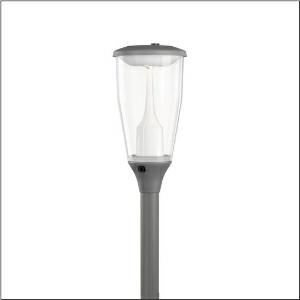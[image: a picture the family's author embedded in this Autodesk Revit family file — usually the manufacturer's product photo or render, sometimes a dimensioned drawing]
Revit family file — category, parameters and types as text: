
# Revit family: dl_11_iq___st1_2a_5xa5565ew14hp00022_746d
name_source: partatom
category: Lighting Fixtures
units: mm (PartAtom-declared; Revit-internal decimal feet)

## family parameters
Cut with Voids When Loaded = No
Host = Face
Light Source = No
Part Type = Normal
Room Calculation Point = No
Round Connector Dimension = Use Diameter
Shared = No

## types (1)
- --- (1 x LED, 4790 lm, 33.5 W, 3000K)
    Apparent Load = 34 VA
    CIE Flux Codes = 23 60 93 95 100
    Color Rendering = 70
    Color Temperature = 3000K
    Default Elevation = 1800 mm
    Description = DL 11 iQ, mast luminaire, Module 540 iQ-SR, primary light control with 3 zone facetted reflector, of plastic, silver coated, highly specular, structured, primary optical cover: cover, of PMMA, transparent, light distribution: ST1.2a, light emission: direct distribution, primary light characteristic: asymmetric, installation type: post-top, LED, High Power LED, rated luminous flux: 4.790lm, luminous efficacy: 143lm/W, light colour: 730, colour temperature: 3000K, control gear: iQ-Street Remote, D4i with power reduction, control: pre-setting: logarithmic dimming characteristic, Street-Remote, Auto-Match, Temp-Guard, Lumen-Switch, Night-Set, Smart-Wire, Light-Fading, Desk-Remote (wireless, voltage-free reading and setting of iQ features in the workshop via application-optimized NFC function/RFID function), optimised constant luminous flux control (CLO 2.0), mains connection: 220..240V, AC, 50/60Hz, connection cable pre-assembled, cable length: 5,5m, start of lifetime: 34W, end of service life: 36W, reduction: 15W, luminaire housing, upper part, of diecast aluminium, coated, SITECO metallic grey (DB 702S), spigot size: 60mm (post-top), mounting height: 3..5m, post-top mast mounting element, of diecast aluminium, coated, SITECO metallic grey (DB 702S), Module 540 iQ-SR, traffic white (RAL 9016), equipment: Power, Smart Interface above and design motion detector below, protection rating (complete): IP65, insulation class (complete): insulation class II (safety insulation), certification: CE, ENEC, ENEC+, VDE, impact resistance: IK07, packaging unit: 1 piece

Light Distribution: ST1.2a
    Height = 665 mm
    Lamp = 1 x LED
    Lamp Light Flux = 4790 lm
    Lamp Power = 33.5 W
    Lamp count = 1
    Length = 334 mm
    Luminous efficacy = 143 lm/W
    Manufacturer = Siteco
    ModVariant = No
    Model = 5XA5565EW14HP00022
    Number of Poles = 1
    OnlyDefault = Yes
    Power Factor = 1
    Product Name = DL 11 iQ | ST1.2a
    Product group = mast luminaire | pylon top
    ProductGroupID = 6100
    Protection Class = Protection class II
    Protection Degree = IP 65
    RLX_Detail_Level = 1
    RLX_Emergency_Light_Flux = 0 lm
    RLX_Emergency_Type = 0
    RLX_Emergency_Type_DB = No
    RlxData = <blob elided: 161305 chars, md5=67ca75c5>
    Socket = socket
    Standby Power = 0 W
    System Light Flux = 4790 lm
    System Power = 34 W
    Type Comments = factory setting: luminous flux: 100 % | dim-lin: 254 | 695 mA
    Type Image = l_1337543.jpg
    URL = http://relux.com
    VarID = @adj_040539
    Voltage = 0 V
    Weight = 0.00 kg
    Width = 0 mm  [stored 0 ft]

note: [stored X ft] marks values corroborated as IEEE doubles in the binary element streams (Revit-internal decimal feet)

## geometry (parser evidence)
native form markers: Blend x4, Sweep x11
no freeform markers — native parametric forms only
